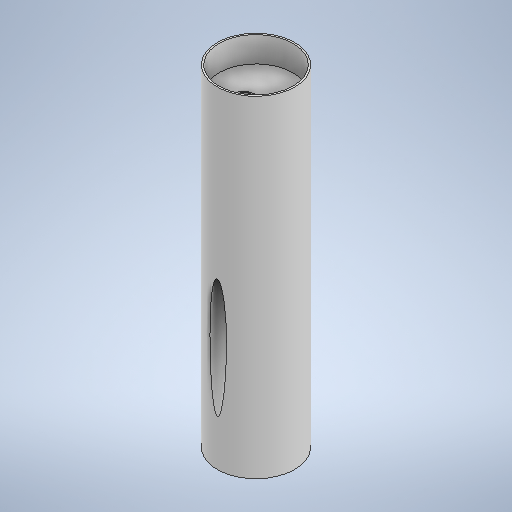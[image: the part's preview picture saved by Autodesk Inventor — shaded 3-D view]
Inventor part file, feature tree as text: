
AUTODESK INVENTOR PART (.ipt)
format: ipt  version: 2025.1 (Build 291241000, 241)  size: 329,728 bytes
history: native  units: mm
features: sketch x6, plane x5, extrude x4, revolve x2, projected_geometry x2, other x1
ambient origin geometry x8: Origin, YZ Plane, XZ Plane, XY Plane, X Axis, Y Axis, Z Axis, Center Point
bodies: Solid1 (feature_tree)
feature tree (20):
  extrude  "Extrusion1"  Depth=67.0mm
  plane  "Work Plane2"
  revolve  "Revolution1"  [1 undecoded]
  revolve  "Revolution3"  [1 undecoded]
  sketch  "Sketch10"  dims[d10=1.5mm d11=8.0mm]
  plane  "Work Plane3"
  sketch  "Sketch11"  dims[d12=23.0mm d13=90.0deg]
  extrude  "Extrusion2"  Depth=8.0mm
  other  "Work Point1"
  plane  "Work Plane4"
  plane  "Work Plane5"
  extrude  "Extrusion3"  TaperAngle=90.0deg  [1 undecoded]
  plane  "Work Plane6"
  extrude  "Extrusion4"  Depth=10.0mm
  sketch  "Sketch1"  dims[d0=70.0mm d1=67.0mm]
  sketch  "Sketch6"  dims[d2=300.0mm d3=0.0mm d7=0.0mm]
  sketch  "Sketch9"  dims[d8=23.0mm d9=1.5mm]
  projected_geometry  "Projected Loop3"
  sketch  "Sketch12"  dims[d24=8.0mm d25=1.5mm d26=1.5mm d27=90.0deg d28=24.0mm d29=1.396263mm d30=18.0mm d31=0.0mm d32=0.0mm d33=15.0mm d34=10.0mm d35=0.0mm d36=35.0mm d37=15.0mm d38=31.0mm d39=10.0mm d40=0.0mm]
  projected_geometry  "Project Cut Edges1"
note: 3 required parameter values undecoded (feature->parameter linkage not recoverable at this tier; creation-order binding heuristic only, values carry confidence <= 0.55)